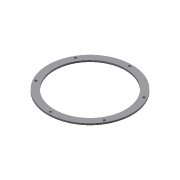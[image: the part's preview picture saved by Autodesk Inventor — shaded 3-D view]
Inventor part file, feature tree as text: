
AUTODESK INVENTOR PART (.ipt)
format: ipt  version: 2015 (Build 190159000, 159)  size: 93,184 bytes
history: native  units: mm
features: extrude x1, sketch x1
ambient origin geometry x8: Origin, YZ Plane, XZ Plane, XY Plane, X Axis, Y Axis, Z Axis, Center Point
bodies: Volumenkörper1 (feature_tree)
feature tree (2):
  extrude  "Extrusion1"  Depth=2.0mm
  sketch  "Skizze1"  dims[d0=86.0mm d1=102.0mm d2=48.0mm d3=3.0mm d4=60.0mm d6=360.0deg d8=2.0mm d9=0.0mm]
